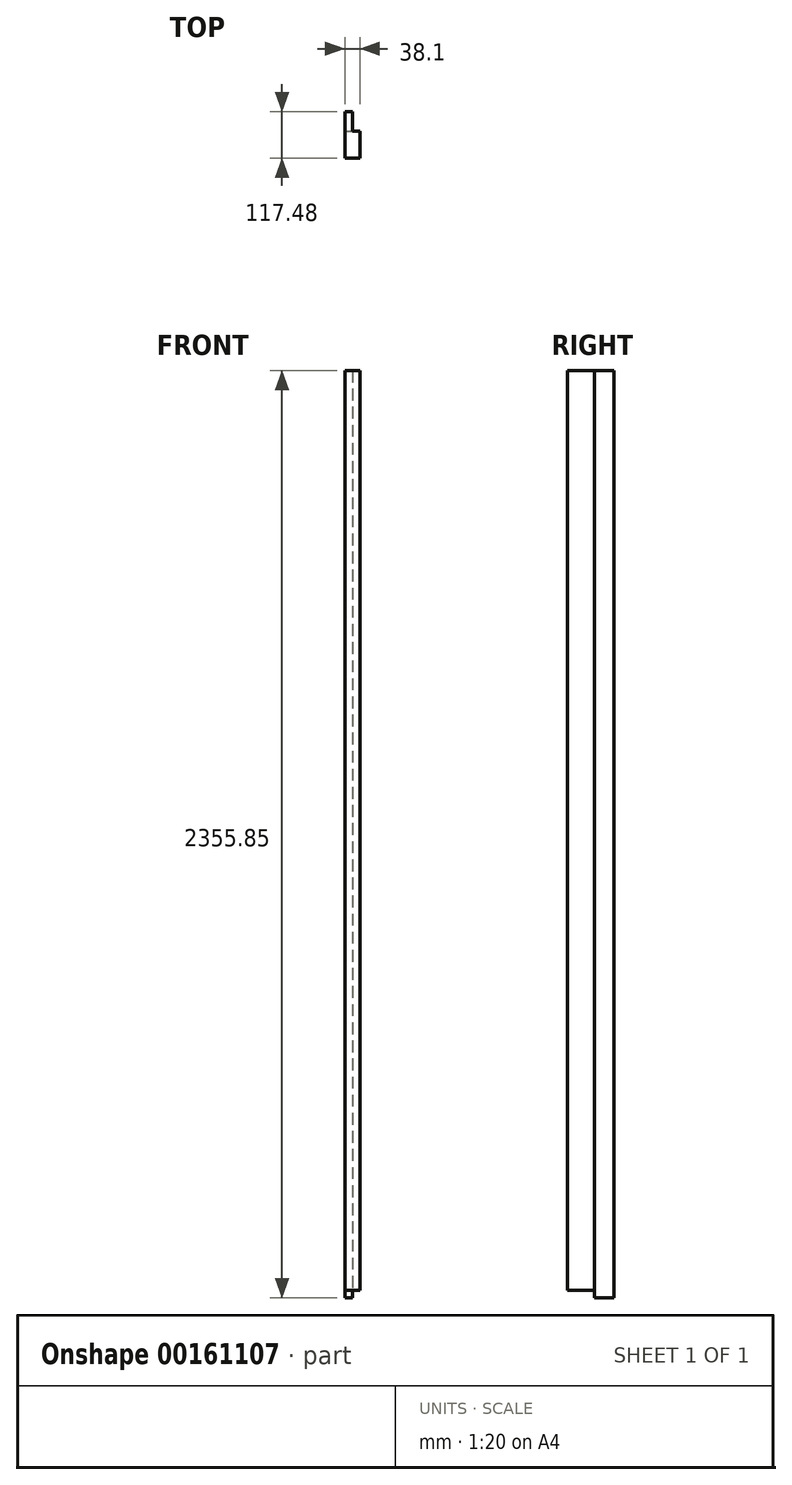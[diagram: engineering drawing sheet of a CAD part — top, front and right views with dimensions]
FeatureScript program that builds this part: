
annotation { "Feature Type Name" : "Feature", "Feature Type Description" : "" }
export const myFeature = defineFeature(function(context is Context, id is Id, definition is map)
    precondition{}
    {
        {
            var Q0;
            Q0=qCreatedBy(makeId("Top.planeOp"),FACE);
            var sketch = newSketch(context, id + "F0", { "sketchPlane" : qUnion([Q0])});
            skLineSegment(sketch, "E0", {"start": v(-2.14, 36.7) * mm, "end": v(-21.19, 36.7) * mm});
            skLineSegment(sketch, "E1", {"start": v(16.91, -80.78) * mm, "end": v(16.91, -12.52) * mm});
            skLineSegment(sketch, "E2", {"start": v(16.91, -12.52) * mm, "end": v(-2.14, -12.52) * mm});
            skLineSegment(sketch, "E3", {"start": v(-2.14, -12.52) * mm, "end": v(-2.14, 36.7) * mm});
            skLineSegment(sketch, "E4", {"start": v(-21.19, 36.7) * mm, "end": v(-21.19, -80.78) * mm});
            skLineSegment(sketch, "E5", {"start": v(-21.19, -80.78) * mm, "end": v(16.91, -80.78) * mm});
            skSolve(sketch);
        }
        {
            var Q0;
            Q0=qSketchRegion(id+"F0",true);
            extrude(context, id + "F1", {"entities" : qUnion([Q0]), "depth" : 2355.85 * mm});
        }
        {
            var Q0;
            Q0=qCreatedBy(makeId("Right.planeOp"),FACE);
            var sketch = newSketch(context, id + "F2", { "sketchPlane" : qUnion([Q0])});
            skLineSegment(sketch, "E6.0", {"start": v(-80.78, 0) * mm, "end": v(-12.52, 0) * mm});
            skLineSegment(sketch, "E7", {"start": v(-80.78, 0) * mm, "end": v(-80.78, 19.05) * mm});
            skLineSegment(sketch, "E8", {"start": v(-80.78, 19.05) * mm, "end": v(-12.52, 19.05) * mm});
            skLineSegment(sketch, "E9", {"start": v(-12.52, 19.05) * mm, "end": v(-12.52, 0) * mm});
            skSolve(sketch);
        }
        {
            var Q0;
            Q0=qSketchRegion(id+"F2",true);
            extrude(context, id + "F3", {"entities" : qUnion([Q0]), "operationType" : NewBodyOperationType.REMOVE, "endBound" : BoundingType.THROUGH_ALL, "oppositeDirection" : true, "depth" : 25.4 * mm, "hasSecondDirection" : true, "secondDirectionBound" : SecondDirectionBoundingType.THROUGH_ALL, "secondDirectionOppositeDirection" : false, "secondDirectionDepth" : 25.4 * mm});
        }
    });
